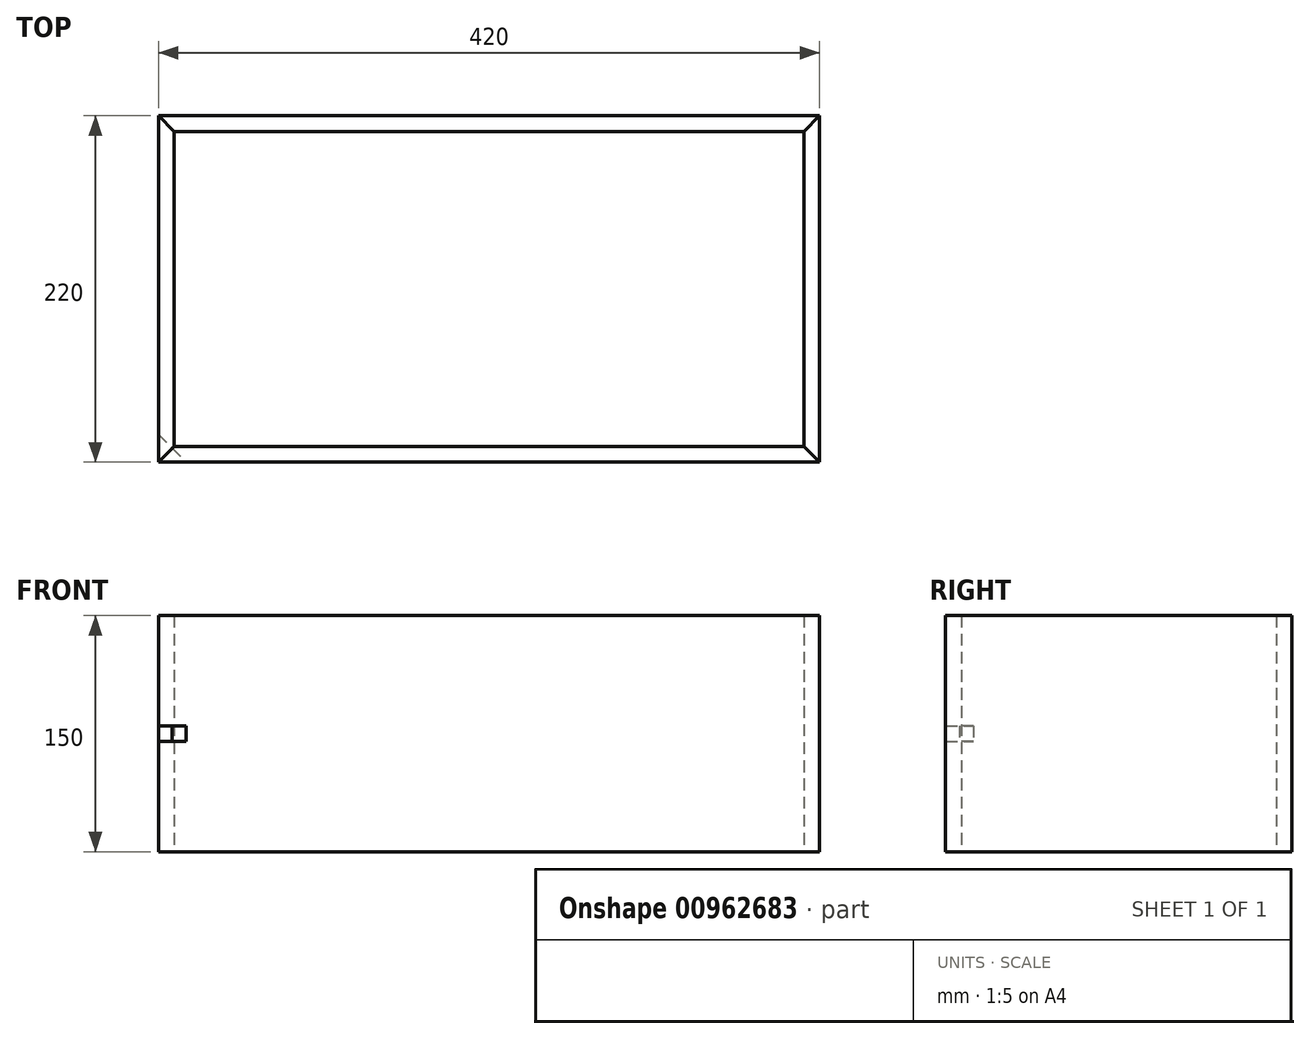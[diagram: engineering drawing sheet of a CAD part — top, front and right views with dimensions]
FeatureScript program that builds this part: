
annotation { "Feature Type Name" : "Feature", "Feature Type Description" : "" }
export const myFeature = defineFeature(function(context is Context, id is Id, definition is map)
    precondition{}
    {
        {
            var Q0;
            Q0=qCreatedBy(makeId("Top.planeOp"),FACE);
            var sketch = newSketch(context, id + "F0", { "sketchPlane" : qUnion([Q0])});
            skLineSegment(sketch, "E0.bottom", {"start": v(-200, 100) * mm, "end": v(200, 100) * mm});
            skLineSegment(sketch, "E0.top", {"start": v(-200, -100) * mm, "end": v(200, -100) * mm});
            skLineSegment(sketch, "E0.left", {"start": v(-200, 100) * mm, "end": v(-200, -100) * mm});
            skLineSegment(sketch, "E0.right", {"start": v(200, 100) * mm, "end": v(200, -100) * mm});
            skPoint(sketch, "E0.middle", {"position": v(0, 0) * mm});
            skLineSegment(sketch, "E1.0", {"start": v(-210, 110) * mm, "end": v(210, 110) * mm});
            skLineSegment(sketch, "E1.1", {"start": v(-210, 110) * mm, "end": v(-210, -110) * mm});
            skLineSegment(sketch, "E1.2", {"start": v(-210, -110) * mm, "end": v(210, -110) * mm});
            skLineSegment(sketch, "E1.3", {"start": v(210, 110) * mm, "end": v(210, -110) * mm});
            skLineSegment(sketch, "E2", {"start": v(-200, 100) * mm, "end": v(-210, 110) * mm});
            skLineSegment(sketch, "E3", {"start": v(200, 100) * mm, "end": v(210, 110) * mm});
            skLineSegment(sketch, "E4", {"start": v(200, -100) * mm, "end": v(210, -110) * mm});
            skLineSegment(sketch, "E5", {"start": v(-200, -100) * mm, "end": v(-210, -110) * mm});
            skSolve(sketch);
        }
        {
            var Q0;
            Q0=makeQuery(id+"F0.imprint","IMPRINT",FACE,{"disambiguationData":[TD([[makeQuery(id+"F0.imprint","IMPRINT",EDGE,{"derivedFrom":sQuery(id+"F0.wireOp",EDGE,"E0.bottom")}),1.0]])]});
            var Q1;
            Q1=makeQuery(id+"F0.imprint","IMPRINT",FACE,{"disambiguationData":[TD([[makeQuery(id+"F0.imprint","IMPRINT",EDGE,{"derivedFrom":sQuery(id+"F0.wireOp",EDGE,"E0.top")}),-1.0]])]});
            extrude(context, id + "F1", {"entities" : qUnion([Q0, Q1]), "depth" : 150 * mm, "offsetDistance" : 25 * mm});
        }
        {
            var Q0;
            Q0=makeQuery(id+"F0.imprint","IMPRINT",FACE,{"disambiguationData":[TD([[makeQuery(id+"F0.imprint","IMPRINT",EDGE,{"derivedFrom":sQuery(id+"F0.wireOp",EDGE,"E0.left")}),-1.0]])]});
            var Q1;
            Q1=makeQuery(id+"F0.imprint","IMPRINT",FACE,{"disambiguationData":[TD([[makeQuery(id+"F0.imprint","IMPRINT",EDGE,{"derivedFrom":sQuery(id+"F0.wireOp",EDGE,"E0.right")}),1.0]])]});
            extrude(context, id + "F2", {"entities" : qUnion([Q0, Q1]), "depth" : 150 * mm, "offsetDistance" : 25 * mm});
        }
        {
            var Q0;
            Q0=makeQuery(id+"F2.opExtrude","SWEPT_FACE",FACE,{"disambiguationData":[OSD([sQuery(id+"F0.wireOp",EDGE,"E5")])]});
            var sketch = newSketch(context, id + "F3", { "sketchPlane" : qUnion([Q0])});
            skLineSegment(sketch, "E6.bottom", {"start": v(-238.77, 80) * mm, "end": v(-213.77, 80) * mm});
            skLineSegment(sketch, "E6.top", {"start": v(-238.77, 70) * mm, "end": v(-213.77, 70) * mm});
            skLineSegment(sketch, "E6.left", {"start": v(-238.77, 80) * mm, "end": v(-238.77, 70) * mm});
            skLineSegment(sketch, "E6.right", {"start": v(-213.77, 80) * mm, "end": v(-213.77, 70) * mm});
            skPoint(sketch, "E6.middle", {"position": v(-226.27, 75) * mm});
            skSolve(sketch);
        }
        {
            var Q0;
            {var subQ0=sQuery(id+"F3.wireOp",EDGE,"E6.right");Q0=makeQuery(id+"F3.imprint","IMPRINT",FACE,{"disambiguationData":[TD([[makeQuery(id+"F3.imprint","IMPRINT",EDGE,{"derivedFrom":subQ0}),-1.0]])]});}
            extrude(context, id + "F4", {"entities" : qUnion([Q0]), "operationType" : NewBodyOperationType.REMOVE, "endBound" : BoundingType.SYMMETRIC, "oppositeDirection" : true, "depth" : 25 * mm, "offsetDistance" : 25 * mm});
        }
        {
            var Q0;
            Q0=makeQuery(id+"F4.boolean.opBoolean","COPY",FACE,{"disambiguationData":[TD([makeQuery(id+"F1.opExtrude","SWEPT_FACE",FACE,{"disambiguationData":[OSD([sQuery(id+"F0.wireOp",EDGE,"E1.2")])]})])],"derivedFrom":makeQuery(id+"F4.opExtrude","SWEPT_FACE",FACE,{"disambiguationData":[OSD([sQuery(id+"F3.wireOp",EDGE,"E6.bottom")])]})});
            var sketch = newSketch(context, id + "F5", { "sketchPlane" : qUnion([Q0])});
            skLineSegment(sketch, "E7", {"start": v(-210, 110) * mm, "end": v(-201.16, 101.16) * mm});
            skLineSegment(sketch, "E8", {"start": v(-210, 110) * mm, "end": v(-210, 110) * mm});
            skSolve(sketch);
        }
        {
            var Q0;
            Q0=makeQuery(id+"F5.imprint","IMPRINT",FACE,{"disambiguationData":[TD([[makeQuery(id+"F5.imprint","IMPRINT",EDGE,{"derivedFrom":sQuery(id+"F5.wireOp",EDGE,"E7")}),1.0]])]});
            var Q1;
            Q1=makeQuery(id+"F4.boolean.opBoolean","COPY",FACE,{"disambiguationData":[TD([makeQuery(id+"F2.opExtrude","SWEPT_FACE",FACE,{"disambiguationData":[OSD([sQuery(id+"F0.wireOp",EDGE,"E1.1")])]})])],"derivedFrom":makeQuery(id+"F4.opExtrude","SWEPT_FACE",FACE,{"disambiguationData":[OSD([sQuery(id+"F3.wireOp",EDGE,"E6.bottom")])]})});
            var Q2;
            Q2=makeQuery(id+"F4.boolean.opBoolean","COPY",FACE,{"disambiguationData":[TD([makeQuery(id+"F1.opExtrude","SWEPT_FACE",FACE,{"disambiguationData":[OSD([sQuery(id+"F0.wireOp",EDGE,"E1.2")])]})])],"derivedFrom":makeQuery(id+"F4.opExtrude","SWEPT_FACE",FACE,{"disambiguationData":[OSD([sQuery(id+"F3.wireOp",EDGE,"E6.top")])]})});
            extrude(context, id + "F6", {"entities" : qUnion([Q0, Q1]), "endBound" : BoundingType.UP_TO_SURFACE, "depth" : 25 * mm, "endBoundEntityFace" : qUnion([Q2]), "offsetDistance" : 25 * mm});
        }
    });
